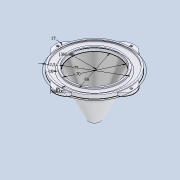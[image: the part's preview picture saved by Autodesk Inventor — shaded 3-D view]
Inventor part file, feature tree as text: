
AUTODESK INVENTOR PART (.ipt)
format: ipt  version: 2020.3 (Build 243373010, 373A)  size: 180,224 bytes
history: native  units: mm
features: extrude x4, sketch x2, hole x1, revolve x1
ambient origin geometry x8: Origin, YZ Plane, XZ Plane, XY Plane, X Axis, Y Axis, Z Axis, Center Point
bodies: Solid1 (feature_tree)
feature tree (8):
  sketch  "Sketch1"  dims[d6=70.0mm d7=68.0mm]
  extrude  "Extrusion1"  Depth=68.0mm
  extrude  "Extrusion2"  Depth=10.0mm
  extrude  "Extrusion3"  Depth=3.0mm
  extrude  "Extrusion4"  Depth=17.0mm
  hole  "Hole1"  [1 undecoded]
  revolve  "Revolution1"  Angle=360.0deg
  sketch  "Sketch2"  dims[d8=75.0mm d11=10.0mm d12=2.5mm d13=17.0mm d14=40.0mm d15=40.0mm d17=360.0deg d19=5.0mm d20=0.0mm d21=3.0mm d22=0.0mm d23=4.0mm d24=0.0mm d25=4.0mm d26=0.0mm d27=13.0mm d28=40.0mm d30=360.0deg d32=3.242mm d33=8.0mm d34=4.0mm d35=2.0mm d36=90.0deg d37=11.8mm d38=0.0mm d39=34.0mm d40=1.0mm d41=60.0mm d42=30.0mm d43=3.0mm d44=3.0mm d45=90.0deg]
note: 1 required parameter value undecoded (feature->parameter linkage not recoverable at this tier; creation-order binding heuristic only, values carry confidence <= 0.55)
